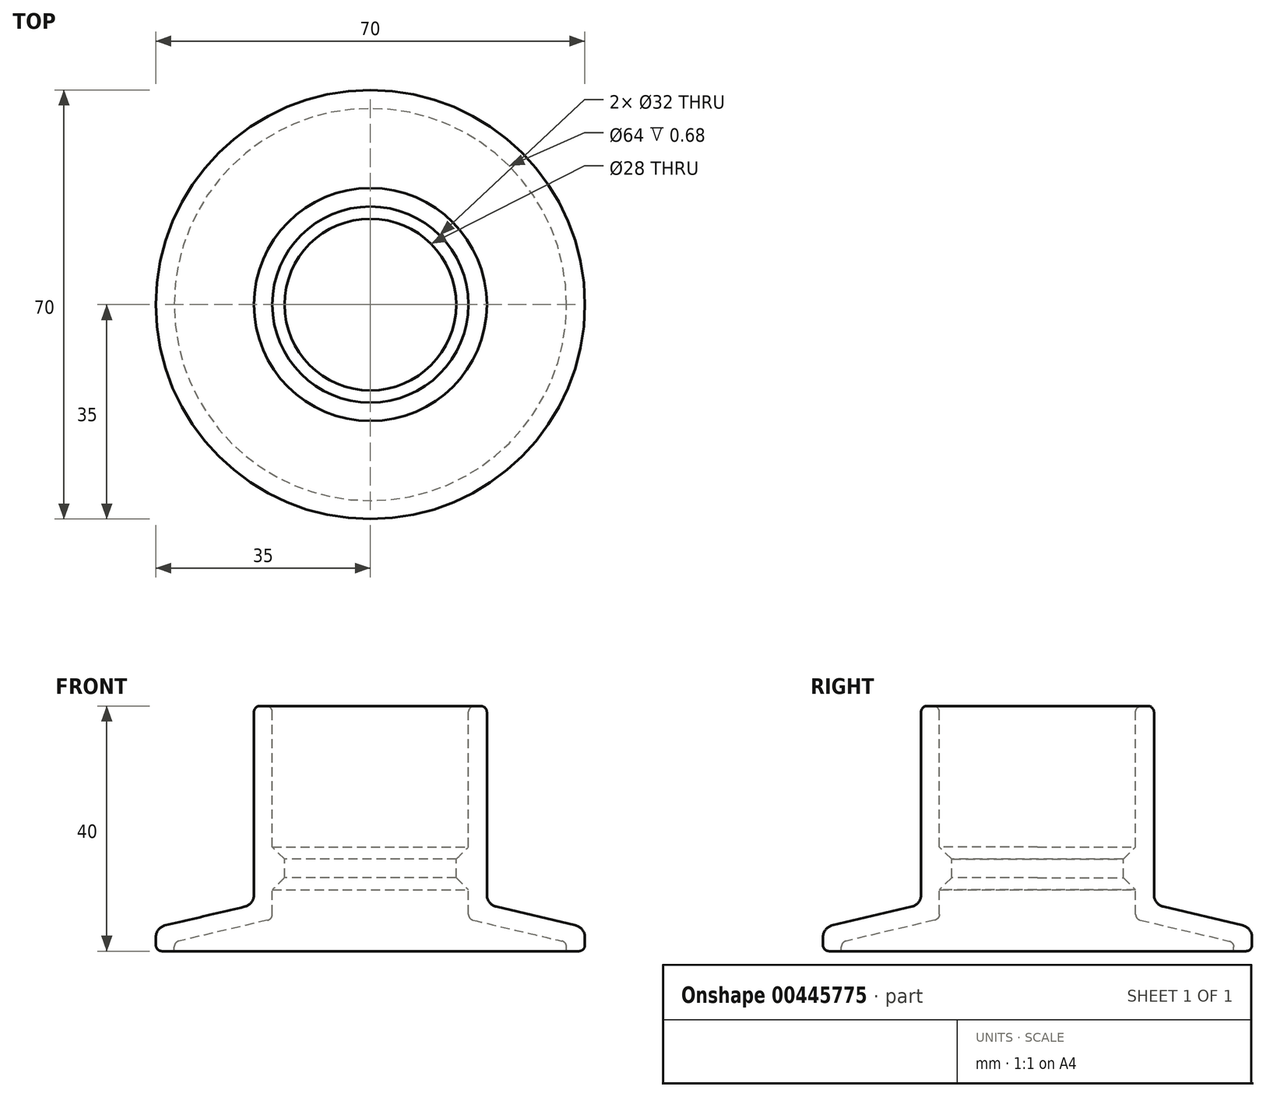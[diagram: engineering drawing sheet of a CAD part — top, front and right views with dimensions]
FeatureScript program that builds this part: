
annotation { "Feature Type Name" : "Feature", "Feature Type Description" : "" }
export const myFeature = defineFeature(function(context is Context, id is Id, definition is map)
    precondition{}
    {
        {
            var Q0;
            Q0=qCreatedBy(makeId("Front.planeOp"),FACE);
            var sketch = newSketch(context, id + "F0", { "sketchPlane" : qUnion([Q0])});
            skLineSegment(sketch, "E0", {"start": v(-32, 0) * mm, "end": v(-35, 0) * mm});
            skLineSegment(sketch, "E1", {"start": v(-16, 40) * mm, "end": v(-16, 15) * mm});
            skLineSegment(sketch, "E2", {"start": v(-16, 40) * mm, "end": v(-19, 40) * mm});
            skLineSegment(sketch, "E3", {"start": v(-19, 40) * mm, "end": v(-19, 7.61) * mm});
            skLineSegment(sketch, "E4", {"start": v(-16, 15) * mm, "end": v(-14, 15) * mm});
            skLineSegment(sketch, "E5", {"start": v(-14, 15) * mm, "end": v(-14, 12) * mm});
            skLineSegment(sketch, "E6", {"start": v(-35, 3.85) * mm, "end": v(-35, 0) * mm});
            skLineSegment(sketch, "E7", {"start": v(-35, 3.85) * mm, "end": v(-19, 7.61) * mm});
            skLineSegment(sketch, "E8", {"start": v(0, 68.49) * mm, "end": v(0, -49.08) * mm, "construction": true});
            skLineSegment(sketch, "E9.0", {"start": v(-32, 1.47) * mm, "end": v(-16, 5.23) * mm});
            skLineSegment(sketch, "E9.1", {"start": v(-32, 1.47) * mm, "end": v(-32, 0) * mm});
            skPoint(sketch, "E10.orphan", {"position": v(-14, 0) * mm});
            skLineSegment(sketch, "E11", {"start": v(-16, 5.23) * mm, "end": v(-16, 12) * mm});
            skLineSegment(sketch, "E12", {"start": v(-16, 12) * mm, "end": v(-14, 12) * mm});
            skSolve(sketch);
        }
        {
            var Q0;
            Q0=makeQuery(id+"F0.imprint","IMPRINT",FACE,{"disambiguationData":[TD([[makeQuery(id+"F0.imprint","IMPRINT",EDGE,{"derivedFrom":sQuery(id+"F0.wireOp",EDGE,"E0")}),-1.0]])]});
            var Q1;
            Q1=sQuery(id+"F0.wireOp",EDGE,"E8");
            revolve(context, id + "F1", {"entities" : qUnion([Q0]), "axis" : qUnion([Q1]), "revolveType" : RevolveType.FULL});
        }
        {
            var Q0;
            Q0=makeQuery(id+"F1.opRevolve","SWEPT_EDGE",EDGE,{"disambiguationData":[OSD([sQuery(id+"F0.wireOp",EDGE,"E1"),sQuery(id+"F0.wireOp",EDGE,"E4")])]});
            chamfer(context, id + "F2", {"entities" : qUnion([Q0]), "width" : 2 * mm, "tangentPropagation" : true});
        }
        {
            var Q0;
            Q0=makeQuery(id+"F1.opRevolve","SWEPT_EDGE",EDGE,{"disambiguationData":[OSD([sQuery(id+"F0.wireOp",EDGE,"E6"),sQuery(id+"F0.wireOp",EDGE,"E7")])]});
            var Q1;
            Q1=makeQuery(id+"F1.opRevolve","SWEPT_EDGE",EDGE,{"disambiguationData":[OSD([sQuery(id+"F0.wireOp",EDGE,"E3"),sQuery(id+"F0.wireOp",EDGE,"E7")])]});
            fillet(context, id + "F3", {"entities" : qUnion([Q0, Q1]), "radius" : 2 * mm, "tangentPropagation" : true, "allowEdgeOverflow" : false});
        }
        {
            var Q0;
            Q0=makeQuery(id+"F1.opRevolve","SWEPT_EDGE",EDGE,{"disambiguationData":[OSD([sQuery(id+"F0.wireOp",EDGE,"E9.0"),sQuery(id+"F0.wireOp",EDGE,"E9.1")])]});
            var Q1;
            Q1=makeQuery(id+"F1.opRevolve","SWEPT_EDGE",EDGE,{"disambiguationData":[OSD([sQuery(id+"F0.wireOp",EDGE,"E9.0"),sQuery(id+"F0.wireOp",EDGE,"E11")])]});
            var Q2;
            Q2=makeQuery(id+"F1.opRevolve","SWEPT_EDGE",EDGE,{"disambiguationData":[OSD([sQuery(id+"F0.wireOp",EDGE,"E0"),sQuery(id+"F0.wireOp",EDGE,"E6")])]});
            var Q3;
            Q3=makeQuery(id+"F1.opRevolve","SWEPT_EDGE",EDGE,{"disambiguationData":[OSD([sQuery(id+"F0.wireOp",EDGE,"E2"),sQuery(id+"F0.wireOp",EDGE,"E3")])]});
            var Q4;
            Q4=makeQuery(id+"F1.opRevolve","SWEPT_EDGE",EDGE,{"disambiguationData":[OSD([sQuery(id+"F0.wireOp",EDGE,"E1"),sQuery(id+"F0.wireOp",EDGE,"E2")])]});
            var Q5;
            Q5=makeQuery(id+"F1.opRevolve","SWEPT_EDGE",EDGE,{"disambiguationData":[OSD([sQuery(id+"F0.wireOp",EDGE,"E0"),sQuery(id+"F0.wireOp",EDGE,"E6")])]});
            fillet(context, id + "F4", {"entities" : qUnion([Q0, Q1, Q2, Q3, Q4, Q5]), "radius" : 1 * mm, "tangentPropagation" : true, "allowEdgeOverflow" : false});
        }
        {
            var Q0;
            Q0=makeQuery(id+"F1.opRevolve","SWEPT_EDGE",EDGE,{"disambiguationData":[OSD([sQuery(id+"F0.wireOp",EDGE,"E11"),sQuery(id+"F0.wireOp",EDGE,"E12")])]});
            chamfer(context, id + "F5", {"entities" : qUnion([Q0]), "width" : 2 * mm, "tangentPropagation" : true});
        }
    });
